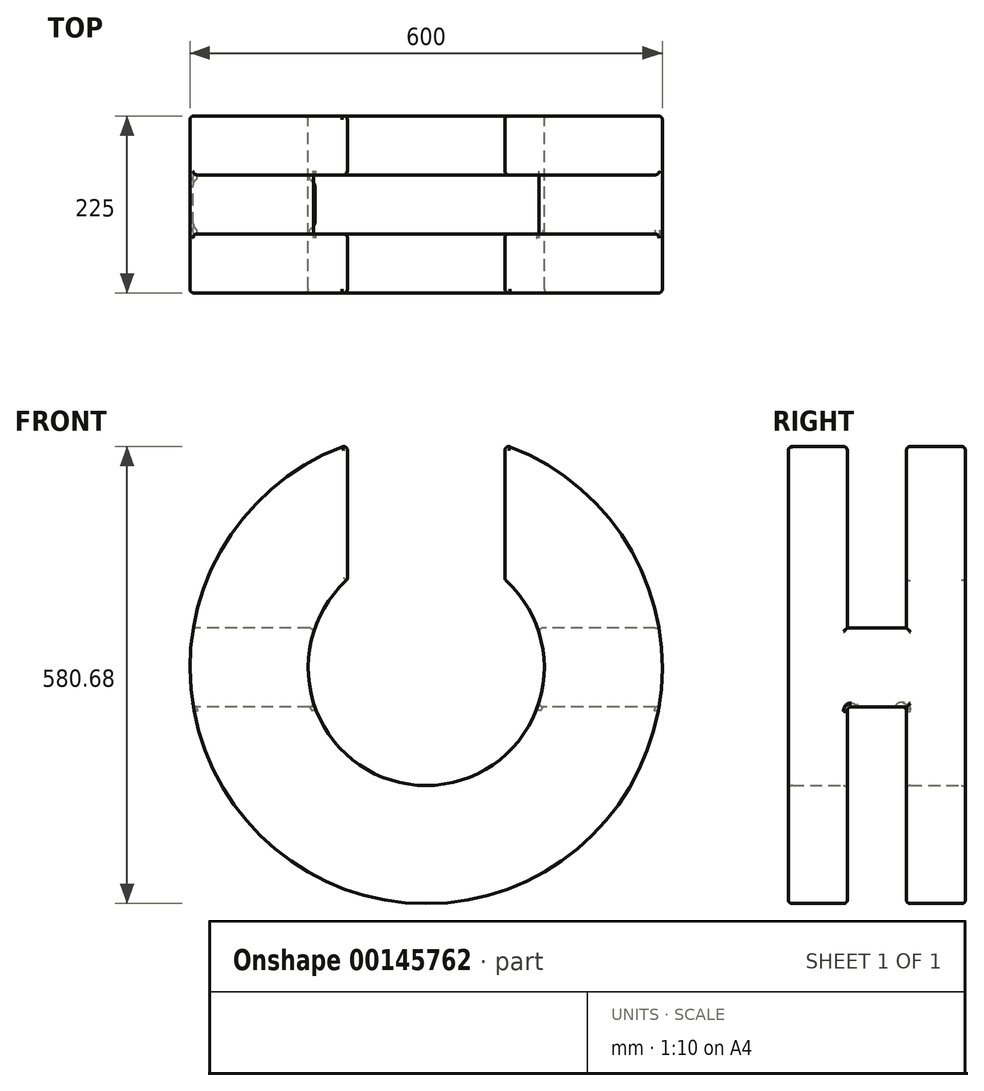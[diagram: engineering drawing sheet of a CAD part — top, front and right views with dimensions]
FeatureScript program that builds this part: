
annotation { "Feature Type Name" : "Feature", "Feature Type Description" : "" }
export const myFeature = defineFeature(function(context is Context, id is Id, definition is map)
    precondition{}
    {
        {
            var Q0;
            Q0=qCreatedBy(makeId("Front.planeOp"),FACE);
            var sketch = newSketch(context, id + "F0", { "sketchPlane" : qUnion([Q0])});
            skArc(sketch, "E0", {"start": v(-100, 111.8) * mm, "mid": v(0, -150) * mm, "end": v(100, 111.8) * mm});
            skArc(sketch, "E1", {"start": v(-100, 282.84) * mm, "mid": v(0, -300) * mm, "end": v(100, 282.84) * mm});
            skLineSegment(sketch, "E2", {"start": v(100, 111.8) * mm, "end": v(100, 282.84) * mm});
            skLineSegment(sketch, "E3", {"start": v(0, 0) * mm, "end": v(0, 388.97) * mm, "construction": true});
            skLineSegment(sketch, "E4.MirrorCS", {"start": v(-100, 111.8) * mm, "end": v(-100, 282.84) * mm});
            skSolve(sketch);
        }
        {
            var Q0;
            Q0=makeQuery(id+"F0.imprint","IMPRINT",FACE,{"disambiguationData":[TD([[makeQuery(id+"F0.imprint","IMPRINT",EDGE,{"derivedFrom":sQuery(id+"F0.wireOp",EDGE,"E0")}),-1.0]])]});
            extrude(context, id + "F1", {"entities" : qUnion([Q0]), "depth" : 225 * mm, "symmetric" : true});
        }
        {
            var Q0;
            Q0=qCreatedBy(makeId("Right.planeOp"),FACE);
            var sketch = newSketch(context, id + "F2", { "sketchPlane" : qUnion([Q0])});
            skLineSegment(sketch, "E5", {"start": v(0, -325) * mm, "end": v(0, 325) * mm, "construction": true});
            skLineSegment(sketch, "E6.bottom", {"start": v(37.5, 325) * mm, "end": v(-37.5, 325) * mm});
            skLineSegment(sketch, "E6.top", {"start": v(37.5, -325) * mm, "end": v(-37.5, -325) * mm});
            skLineSegment(sketch, "E6.left", {"start": v(37.5, 325) * mm, "end": v(37.5, 50) * mm});
            skLineSegment(sketch, "E6.right", {"start": v(-37.5, 325) * mm, "end": v(-37.5, 50) * mm});
            skPoint(sketch, "E6.middle", {"position": v(0, 0) * mm});
            skLineSegment(sketch, "E7", {"start": v(0, 0) * mm, "end": v(108.56, 0) * mm, "construction": true});
            skLineSegment(sketch, "E8.0", {"start": v(0, -50) * mm, "end": v(37.5, -50) * mm});
            skLineSegment(sketch, "E9.0", {"start": v(0, 50) * mm, "end": v(37.5, 50) * mm});
            skLineSegment(sketch, "E10.MirrorCS", {"start": v(0, 50) * mm, "end": v(-37.5, 50) * mm});
            skLineSegment(sketch, "E11.MirrorCS", {"start": v(0, -50) * mm, "end": v(-37.5, -50) * mm});
            skLineSegment(sketch, "E12.trimOffspring", {"start": v(-37.5, -50) * mm, "end": v(-37.5, -325) * mm});
            skLineSegment(sketch, "E13.trimOffspring", {"start": v(37.5, -50) * mm, "end": v(37.5, -325) * mm});
            skPoint(sketch, "E14.orphan", {"position": v(108.56, 50) * mm});
            skPoint(sketch, "E15.orphan", {"position": v(-108.56, 50) * mm});
            skPoint(sketch, "E16.orphan", {"position": v(-108.56, -50) * mm});
            skPoint(sketch, "E17.orphan", {"position": v(108.56, -50) * mm});
            skSolve(sketch);
        }
        {
            var Q0;
            Q0=makeQuery(id+"F2.imprint","IMPRINT",FACE,{"disambiguationData":[TD([[makeQuery(id+"F2.imprint","IMPRINT",EDGE,{"derivedFrom":sQuery(id+"F2.wireOp",EDGE,"E6.bottom")}),1.0]])]});
            var Q1;
            Q1=makeQuery(id+"F2.imprint","IMPRINT",FACE,{"disambiguationData":[TD([[makeQuery(id+"F2.imprint","IMPRINT",EDGE,{"derivedFrom":sQuery(id+"F2.wireOp",EDGE,"E6.top")}),-1.0]])]});
            extrude(context, id + "F3", {"entities" : qUnion([Q0, Q1]), "operationType" : NewBodyOperationType.REMOVE, "depth" : 650 * mm, "symmetric" : true});
        }
        {
            var Q0;
            Q0=makeQuery(id+"F1.opExtrude","CAP_EDGE",EDGE,{"disambiguationData":[OSD([sQuery(id+"F0.wireOp",EDGE,"E1")])],"isStart":false});
            fillet(context, id + "F4", {"entities" : qUnion([Q0]), "radius" : 5 * mm, "tangentPropagation" : true, "allowEdgeOverflow" : false});
        }
        {
            var Q0;
            Q0=makeQuery(id+"F1.opExtrude","CAP_EDGE",EDGE,{"disambiguationData":[OSD([sQuery(id+"F0.wireOp",EDGE,"E0")])],"isStart":false});
            var Q1;
            Q1=makeQuery(id+"F3.boolean.opBoolean","INTERSECT",EDGE,{"disambiguationData":[OD(0.0)],"derivedFrom":[makeQuery(id+"F1.opExtrude","SWEPT_FACE",FACE,{"disambiguationData":[OSD([sQuery(id+"F0.wireOp",EDGE,"E0")])]}),makeQuery(id+"F3.opExtrude","SWEPT_FACE",FACE,{"disambiguationData":[OSD([sQuery(id+"F2.wireOp",EDGE,"E6.right")])]})]});
            var Q2;
            {var subQ0=sQuery(id+"F0.wireOp",EDGE,"E0");var subQ1=sQuery(id+"F0.wireOp",EDGE,"E4.MirrorCS");Q2=makeQuery(id+"F3.boolean.opBoolean","SPLIT",EDGE,{"disambiguationData":[TD([makeQuery(id+"F3.opExtrude","SWEPT_FACE",FACE,{"disambiguationData":[OSD([sQuery(id+"F2.wireOp",EDGE,"E6.right")])]})])],"derivedFrom":makeQuery(id+"F1.opExtrude","SWEPT_EDGE",EDGE,{"disambiguationData":[OSD([subQ0,subQ1])]})});}
            var Q3;
            Q3=makeQuery(id+"F1.opExtrude","CAP_EDGE",EDGE,{"disambiguationData":[OSD([sQuery(id+"F0.wireOp",EDGE,"E4.MirrorCS")])],"isStart":false});
            var Q4;
            {var subQ0=sQuery(id+"F0.wireOp",EDGE,"E4.MirrorCS");var subQ1=sQuery(id+"F0.wireOp",EDGE,"E1");Q4=makeQuery(id+"F3.boolean.opBoolean","SPLIT",EDGE,{"disambiguationData":[TD([makeQuery(id+"F3.opExtrude","SWEPT_FACE",FACE,{"disambiguationData":[OSD([sQuery(id+"F2.wireOp",EDGE,"E6.right")])]})])],"derivedFrom":makeQuery(id+"F1.opExtrude","SWEPT_EDGE",EDGE,{"disambiguationData":[OSD([subQ1,subQ0])]})});}
            var Q5;
            Q5=makeQuery(id+"F3.boolean.opBoolean","INTERSECT",EDGE,{"derivedFrom":[makeQuery(id+"F1.opExtrude","SWEPT_FACE",FACE,{"disambiguationData":[OSD([sQuery(id+"F0.wireOp",EDGE,"E4.MirrorCS")])]}),makeQuery(id+"F3.opExtrude","SWEPT_FACE",FACE,{"disambiguationData":[OSD([sQuery(id+"F2.wireOp",EDGE,"E6.right")])]})]});
            var Q6;
            Q6=makeQuery(id+"F3.boolean.opBoolean","INTERSECT",EDGE,{"disambiguationData":[OD(1.0)],"derivedFrom":[makeQuery(id+"F1.opExtrude","SWEPT_FACE",FACE,{"disambiguationData":[OSD([sQuery(id+"F0.wireOp",EDGE,"E0")])]}),makeQuery(id+"F3.opExtrude","SWEPT_FACE",FACE,{"disambiguationData":[OSD([sQuery(id+"F2.wireOp",EDGE,"E9.0"),sQuery(id+"F2.wireOp",EDGE,"E10.MirrorCS")])]})]});
            var Q7;
            Q7=makeQuery(id+"F3.boolean.opBoolean","INTERSECT",EDGE,{"disambiguationData":[OD(0.0)],"derivedFrom":[makeQuery(id+"F1.opExtrude","SWEPT_FACE",FACE,{"disambiguationData":[OSD([sQuery(id+"F0.wireOp",EDGE,"E0")])]}),makeQuery(id+"F3.opExtrude","SWEPT_FACE",FACE,{"disambiguationData":[OSD([sQuery(id+"F2.wireOp",EDGE,"E6.left")])]})]});
            var Q8;
            Q8=makeQuery(id+"F3.boolean.opBoolean","INTERSECT",EDGE,{"derivedFrom":[makeQuery(id+"F1.opExtrude","SWEPT_FACE",FACE,{"disambiguationData":[OSD([sQuery(id+"F0.wireOp",EDGE,"E4.MirrorCS")])]}),makeQuery(id+"F3.opExtrude","SWEPT_FACE",FACE,{"disambiguationData":[OSD([sQuery(id+"F2.wireOp",EDGE,"E6.left")])]})]});
            var Q9;
            Q9=makeQuery(id+"F3.boolean.opBoolean","INTERSECT",EDGE,{"disambiguationData":[OD(0.0)],"derivedFrom":[makeQuery(id+"F1.opExtrude","SWEPT_FACE",FACE,{"disambiguationData":[OSD([sQuery(id+"F0.wireOp",EDGE,"E1")])]}),makeQuery(id+"F3.opExtrude","SWEPT_FACE",FACE,{"disambiguationData":[OSD([sQuery(id+"F2.wireOp",EDGE,"E6.left")])]})]});
            var Q10;
            {var subQ0=sQuery(id+"F0.wireOp",EDGE,"E4.MirrorCS");var subQ1=sQuery(id+"F0.wireOp",EDGE,"E1");Q10=makeQuery(id+"F3.boolean.opBoolean","SPLIT",EDGE,{"disambiguationData":[TD([makeQuery(id+"F3.opExtrude","SWEPT_FACE",FACE,{"disambiguationData":[OSD([sQuery(id+"F2.wireOp",EDGE,"E6.left")])]})])],"derivedFrom":makeQuery(id+"F1.opExtrude","SWEPT_EDGE",EDGE,{"disambiguationData":[OSD([subQ1,subQ0])]})});}
            var Q11;
            Q11=makeQuery(id+"F1.opExtrude","CAP_EDGE",EDGE,{"disambiguationData":[OSD([sQuery(id+"F0.wireOp",EDGE,"E1")])],"isStart":true});
            var Q12;
            Q12=makeQuery(id+"F3.boolean.opBoolean","INTERSECT",EDGE,{"disambiguationData":[OD(1.0)],"derivedFrom":[makeQuery(id+"F1.opExtrude","SWEPT_FACE",FACE,{"disambiguationData":[OSD([sQuery(id+"F0.wireOp",EDGE,"E1")])]}),makeQuery(id+"F3.opExtrude","SWEPT_FACE",FACE,{"disambiguationData":[OSD([sQuery(id+"F2.wireOp",EDGE,"E9.0"),sQuery(id+"F2.wireOp",EDGE,"E10.MirrorCS")])]})]});
            var Q13;
            Q13=makeQuery(id+"F3.boolean.opBoolean","INTERSECT",EDGE,{"disambiguationData":[OD(0.0)],"derivedFrom":[makeQuery(id+"F1.opExtrude","SWEPT_FACE",FACE,{"disambiguationData":[OSD([sQuery(id+"F0.wireOp",EDGE,"E1")])]}),makeQuery(id+"F3.opExtrude","SWEPT_FACE",FACE,{"disambiguationData":[OSD([sQuery(id+"F2.wireOp",EDGE,"E6.right")])]})]});
            var Q14;
            Q14=makeQuery(id+"F1.opExtrude","CAP_EDGE",EDGE,{"disambiguationData":[OSD([sQuery(id+"F0.wireOp",EDGE,"E0")])],"isStart":true});
            var Q15;
            Q15=makeQuery(id+"F1.opExtrude","CAP_EDGE",EDGE,{"disambiguationData":[OSD([sQuery(id+"F0.wireOp",EDGE,"E2")])],"isStart":true});
            var Q16;
            {var subQ0=sQuery(id+"F0.wireOp",EDGE,"E2");var subQ1=sQuery(id+"F0.wireOp",EDGE,"E1");Q16=makeQuery(id+"F3.boolean.opBoolean","SPLIT",EDGE,{"disambiguationData":[TD([makeQuery(id+"F3.opExtrude","SWEPT_FACE",FACE,{"disambiguationData":[OSD([sQuery(id+"F2.wireOp",EDGE,"E6.left")])]})])],"derivedFrom":makeQuery(id+"F1.opExtrude","SWEPT_EDGE",EDGE,{"disambiguationData":[OSD([subQ1,subQ0])]})});}
            var Q17;
            Q17=makeQuery(id+"F3.boolean.opBoolean","INTERSECT",EDGE,{"disambiguationData":[OD(1.0)],"derivedFrom":[makeQuery(id+"F1.opExtrude","SWEPT_FACE",FACE,{"disambiguationData":[OSD([sQuery(id+"F0.wireOp",EDGE,"E1")])]}),makeQuery(id+"F3.opExtrude","SWEPT_FACE",FACE,{"disambiguationData":[OSD([sQuery(id+"F2.wireOp",EDGE,"E6.left")])]})]});
            var Q18;
            Q18=makeQuery(id+"F3.boolean.opBoolean","INTERSECT",EDGE,{"disambiguationData":[OD(0.0)],"derivedFrom":[makeQuery(id+"F1.opExtrude","SWEPT_FACE",FACE,{"disambiguationData":[OSD([sQuery(id+"F0.wireOp",EDGE,"E1")])]}),makeQuery(id+"F3.opExtrude","SWEPT_FACE",FACE,{"disambiguationData":[OSD([sQuery(id+"F2.wireOp",EDGE,"E9.0"),sQuery(id+"F2.wireOp",EDGE,"E10.MirrorCS")])]})]});
            var Q19;
            Q19=makeQuery(id+"F3.boolean.opBoolean","INTERSECT",EDGE,{"disambiguationData":[OD(1.0)],"derivedFrom":[makeQuery(id+"F1.opExtrude","SWEPT_FACE",FACE,{"disambiguationData":[OSD([sQuery(id+"F0.wireOp",EDGE,"E1")])]}),makeQuery(id+"F3.opExtrude","SWEPT_FACE",FACE,{"disambiguationData":[OSD([sQuery(id+"F2.wireOp",EDGE,"E6.right")])]})]});
            var Q20;
            {var subQ0=sQuery(id+"F0.wireOp",EDGE,"E2");var subQ1=sQuery(id+"F0.wireOp",EDGE,"E1");Q20=makeQuery(id+"F3.boolean.opBoolean","SPLIT",EDGE,{"disambiguationData":[TD([makeQuery(id+"F3.opExtrude","SWEPT_FACE",FACE,{"disambiguationData":[OSD([sQuery(id+"F2.wireOp",EDGE,"E6.right")])]})])],"derivedFrom":makeQuery(id+"F1.opExtrude","SWEPT_EDGE",EDGE,{"disambiguationData":[OSD([subQ1,subQ0])]})});}
            var Q21;
            Q21=makeQuery(id+"F1.opExtrude","CAP_EDGE",EDGE,{"disambiguationData":[OSD([sQuery(id+"F0.wireOp",EDGE,"E2")])],"isStart":false});
            var Q22;
            {var subQ0=sQuery(id+"F0.wireOp",EDGE,"E0");var subQ1=sQuery(id+"F0.wireOp",EDGE,"E2");Q22=makeQuery(id+"F3.boolean.opBoolean","SPLIT",EDGE,{"disambiguationData":[TD([makeQuery(id+"F3.opExtrude","SWEPT_FACE",FACE,{"disambiguationData":[OSD([sQuery(id+"F2.wireOp",EDGE,"E6.right")])]})])],"derivedFrom":makeQuery(id+"F1.opExtrude","SWEPT_EDGE",EDGE,{"disambiguationData":[OSD([subQ0,subQ1])]})});}
            var Q23;
            Q23=makeQuery(id+"F3.boolean.opBoolean","INTERSECT",EDGE,{"derivedFrom":[makeQuery(id+"F1.opExtrude","SWEPT_FACE",FACE,{"disambiguationData":[OSD([sQuery(id+"F0.wireOp",EDGE,"E2")])]}),makeQuery(id+"F3.opExtrude","SWEPT_FACE",FACE,{"disambiguationData":[OSD([sQuery(id+"F2.wireOp",EDGE,"E6.right")])]})]});
            var Q24;
            Q24=makeQuery(id+"F3.boolean.opBoolean","INTERSECT",EDGE,{"disambiguationData":[OD(1.0)],"derivedFrom":[makeQuery(id+"F1.opExtrude","SWEPT_FACE",FACE,{"disambiguationData":[OSD([sQuery(id+"F0.wireOp",EDGE,"E0")])]}),makeQuery(id+"F3.opExtrude","SWEPT_FACE",FACE,{"disambiguationData":[OSD([sQuery(id+"F2.wireOp",EDGE,"E6.left")])]})]});
            var Q25;
            Q25=makeQuery(id+"F3.boolean.opBoolean","INTERSECT",EDGE,{"disambiguationData":[OD(0.0)],"derivedFrom":[makeQuery(id+"F1.opExtrude","SWEPT_FACE",FACE,{"disambiguationData":[OSD([sQuery(id+"F0.wireOp",EDGE,"E0")])]}),makeQuery(id+"F3.opExtrude","SWEPT_FACE",FACE,{"disambiguationData":[OSD([sQuery(id+"F2.wireOp",EDGE,"E9.0"),sQuery(id+"F2.wireOp",EDGE,"E10.MirrorCS")])]})]});
            var Q26;
            {var subQ0=sQuery(id+"F0.wireOp",EDGE,"E0");var subQ1=sQuery(id+"F0.wireOp",EDGE,"E2");Q26=makeQuery(id+"F3.boolean.opBoolean","SPLIT",EDGE,{"disambiguationData":[TD([makeQuery(id+"F3.opExtrude","SWEPT_FACE",FACE,{"disambiguationData":[OSD([sQuery(id+"F2.wireOp",EDGE,"E6.left")])]})])],"derivedFrom":makeQuery(id+"F1.opExtrude","SWEPT_EDGE",EDGE,{"disambiguationData":[OSD([subQ0,subQ1])]})});}
            var Q27;
            Q27=makeQuery(id+"F3.boolean.opBoolean","INTERSECT",EDGE,{"derivedFrom":[makeQuery(id+"F1.opExtrude","SWEPT_FACE",FACE,{"disambiguationData":[OSD([sQuery(id+"F0.wireOp",EDGE,"E2")])]}),makeQuery(id+"F3.opExtrude","SWEPT_FACE",FACE,{"disambiguationData":[OSD([sQuery(id+"F2.wireOp",EDGE,"E6.left")])]})]});
            var Q28;
            Q28=makeQuery(id+"F3.boolean.opBoolean","INTERSECT",EDGE,{"disambiguationData":[OD(1.0)],"derivedFrom":[makeQuery(id+"F1.opExtrude","SWEPT_FACE",FACE,{"disambiguationData":[OSD([sQuery(id+"F0.wireOp",EDGE,"E0")])]}),makeQuery(id+"F3.opExtrude","SWEPT_FACE",FACE,{"disambiguationData":[OSD([sQuery(id+"F2.wireOp",EDGE,"E8.0"),sQuery(id+"F2.wireOp",EDGE,"E11.MirrorCS")])]})]});
            var Q29;
            Q29=makeQuery(id+"F3.boolean.opBoolean","INTERSECT",EDGE,{"derivedFrom":[makeQuery(id+"F1.opExtrude","SWEPT_FACE",FACE,{"disambiguationData":[OSD([sQuery(id+"F0.wireOp",EDGE,"E0")])]}),makeQuery(id+"F3.opExtrude","SWEPT_FACE",FACE,{"disambiguationData":[OSD([sQuery(id+"F2.wireOp",EDGE,"E13.trimOffspring")])]})]});
            var Q30;
            Q30=makeQuery(id+"F3.boolean.opBoolean","INTERSECT",EDGE,{"derivedFrom":[makeQuery(id+"F1.opExtrude","SWEPT_FACE",FACE,{"disambiguationData":[OSD([sQuery(id+"F0.wireOp",EDGE,"E0")])]}),makeQuery(id+"F3.opExtrude","SWEPT_FACE",FACE,{"disambiguationData":[OSD([sQuery(id+"F2.wireOp",EDGE,"E12.trimOffspring")])]})]});
            var Q31;
            Q31=makeQuery(id+"F3.boolean.opBoolean","INTERSECT",EDGE,{"derivedFrom":[makeQuery(id+"F1.opExtrude","SWEPT_FACE",FACE,{"disambiguationData":[OSD([sQuery(id+"F0.wireOp",EDGE,"E1")])]}),makeQuery(id+"F3.opExtrude","SWEPT_FACE",FACE,{"disambiguationData":[OSD([sQuery(id+"F2.wireOp",EDGE,"E12.trimOffspring")])]})]});
            var Q32;
            Q32=makeQuery(id+"F3.boolean.opBoolean","COPY",EDGE,{"disambiguationData":[OD(0.0)],"derivedFrom":makeQuery(id+"F3.opExtrude","SWEPT_EDGE",EDGE,{"disambiguationData":[OSD([sQuery(id+"F2.wireOp",EDGE,"E11.MirrorCS"),sQuery(id+"F2.wireOp",EDGE,"E12.trimOffspring")])]})});
            var Q33;
            Q33=makeQuery(id+"F3.boolean.opBoolean","INTERSECT",EDGE,{"derivedFrom":[makeQuery(id+"F1.opExtrude","SWEPT_FACE",FACE,{"disambiguationData":[OSD([sQuery(id+"F0.wireOp",EDGE,"E1")])]}),makeQuery(id+"F3.opExtrude","SWEPT_FACE",FACE,{"disambiguationData":[OSD([sQuery(id+"F2.wireOp",EDGE,"E13.trimOffspring")])]})]});
            var Q34;
            Q34=makeQuery(id+"F3.boolean.opBoolean","INTERSECT",EDGE,{"disambiguationData":[OD(1.0)],"derivedFrom":[makeQuery(id+"F1.opExtrude","SWEPT_FACE",FACE,{"disambiguationData":[OSD([sQuery(id+"F0.wireOp",EDGE,"E1")])]}),makeQuery(id+"F3.opExtrude","SWEPT_FACE",FACE,{"disambiguationData":[OSD([sQuery(id+"F2.wireOp",EDGE,"E8.0"),sQuery(id+"F2.wireOp",EDGE,"E11.MirrorCS")])]})]});
            var Q35;
            Q35=makeQuery(id+"F3.boolean.opBoolean","COPY",EDGE,{"disambiguationData":[OD(0.0)],"derivedFrom":makeQuery(id+"F3.opExtrude","SWEPT_EDGE",EDGE,{"disambiguationData":[OSD([sQuery(id+"F2.wireOp",EDGE,"E8.0"),sQuery(id+"F2.wireOp",EDGE,"E13.trimOffspring")])]})});
            var Q36;
            Q36=makeQuery(id+"F3.boolean.opBoolean","COPY",EDGE,{"disambiguationData":[OD(1.0)],"derivedFrom":makeQuery(id+"F3.opExtrude","SWEPT_EDGE",EDGE,{"disambiguationData":[OSD([sQuery(id+"F2.wireOp",EDGE,"E11.MirrorCS"),sQuery(id+"F2.wireOp",EDGE,"E12.trimOffspring")])]})});
            fillet(context, id + "F5", {"entities" : qUnion([Q0, Q1, Q2, Q3, Q4, Q5, Q6, Q7, Q8, Q9, Q10, Q11, Q12, Q13, Q14, Q15, Q16, Q17, Q18, Q19, Q20, Q21, Q22, Q23, Q24, Q25, Q26, Q27, Q28, Q29, Q30, Q31, Q32, Q33, Q34, Q35, Q36]), "radius" : 5 * mm, "tangentPropagation" : true, "allowEdgeOverflow" : false});
        }
        {
            var Q0;
            Q0=makeQuery(id+"F1.opExtrude","CAP_EDGE",EDGE,{"disambiguationData":[OSD([sQuery(id+"F0.wireOp",EDGE,"E4.MirrorCS")])],"isStart":true});
            var Q1;
            {var subQ1=sQuery(id+"F0.wireOp",EDGE,"E4.MirrorCS");var subQ3=makeQuery(id+"F3.opExtrude","SWEPT_FACE",FACE,{"disambiguationData":[OSD([sQuery(id+"F2.wireOp",EDGE,"E6.left")])]});var subQ4=makeQuery(id+"F1.opExtrude","SWEPT_FACE",FACE,{"disambiguationData":[OSD([subQ1])]});Q1=makeQuery(id+"F5.opFillet","BLEND_EDGE",EDGE,{"blendedFrom":[makeQuery(id+"F3.boolean.opBoolean","INTERSECT",EDGE,{"derivedFrom":[subQ4,subQ3]}),makeQuery(id+"F3.boolean.opBoolean","SPLIT",FACE,{"disambiguationData":[TD([subQ3])],"derivedFrom":subQ4})],"blendedInto":[makeQuery(id+"F3.boolean.opBoolean","SPLIT",FACE,{"disambiguationData":[TD([subQ3])],"derivedFrom":subQ4})]});}
            var Q2;
            {var subQ0=sQuery(id+"F0.wireOp",EDGE,"E0");var subQ1=sQuery(id+"F0.wireOp",EDGE,"E4.MirrorCS");Q2=makeQuery(id+"F3.boolean.opBoolean","SPLIT",EDGE,{"disambiguationData":[TD([makeQuery(id+"F3.opExtrude","SWEPT_FACE",FACE,{"disambiguationData":[OSD([sQuery(id+"F2.wireOp",EDGE,"E6.left")])]})])],"derivedFrom":makeQuery(id+"F1.opExtrude","SWEPT_EDGE",EDGE,{"disambiguationData":[OSD([subQ0,subQ1])]})});}
            fillet(context, id + "F6", {"entities" : qUnion([Q0, Q1, Q2]), "radius" : 5 * mm, "tangentPropagation" : true, "allowEdgeOverflow" : false});
        }
    });
